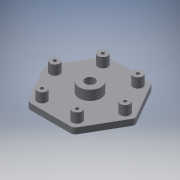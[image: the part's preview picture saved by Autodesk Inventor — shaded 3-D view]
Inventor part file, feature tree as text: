
AUTODESK INVENTOR PART (.ipt)
format: ipt  version: 2017 (Build 210142000, 142)  size: 188,928 bytes
history: native  units: mm
features: extrude x4, sketch x4, projected_geometry x2, fillet x1
ambient origin geometry x8: Origin, YZ Plane, XZ Plane, XY Plane, X Axis, Y Axis, Z Axis, Center Point
bodies: Solid1 (feature_tree)
feature tree (11):
  extrude  "Extrusion1"  Depth=8.0mm
  fillet  "Fillet1"  Radius=8.0mm
  extrude  "Extrusion2"  Depth=8.0mm
  extrude  "Extrusion3"  Depth=4.0mm
  extrude  "Extrusion4"  Depth=8.0mm TaperAngle=0.0deg
  sketch  "Sketch1"  dims[d0=22.0mm d1=50.229473mm d2=8.0mm]
  sketch  "Sketch2"  dims[d3=65.0mm d4=8.0mm]
  projected_geometry  "Projected Loop1"
  sketch  "Sketch3"  dims[d5=5.0mm d6=0.0mm d7=4.0mm]
  projected_geometry  "Projected Loop2"
  sketch  "Sketch4"  dims[d8=5.0mm d9=8.0mm d10=0.0mm d11=8.0mm d12=0.0mm d13=80.0mm d14=2.7mm d15=10.0mm d16=0.0mm d17=75.055535mm]
